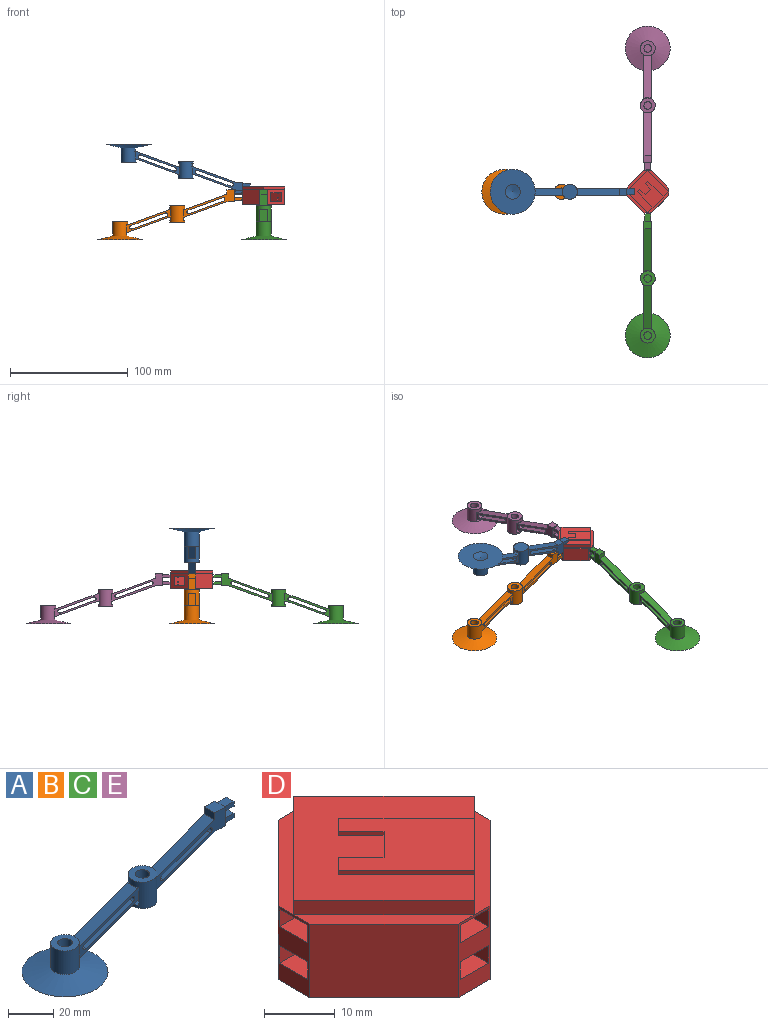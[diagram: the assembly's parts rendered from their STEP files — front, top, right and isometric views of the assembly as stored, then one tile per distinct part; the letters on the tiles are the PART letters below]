
ASSEMBLY  parts=5 mates=1
PART A: 57 faces, bbox 122.4x38.1x42.6 mm
  f0: cylinder r=6.35mm len=14.29mm, axis (0,0,-1), area 443.4mm2, adj f3,f4,f5,f18,f22,f24,f25,f28
  f1: cylinder r=6.35mm len=12.7mm, axis (0,0,-1), area 443.4mm2, adj f3,f4,f8,f9,f11,f12,f26,f27
  f2: cylinder r=3.23mm len=12.7mm, axis (0,0,-1), area 228.9mm2, adj f9,f10,f13,f26,f27
  f3: plane 37.5x19.38mm, normal (0,-1,0), area 137.5mm2, adj f0,f1,f5,f12,f13,f14,f15,f16
  f4: plane 37.5x19.38mm, normal (0,1,0), area 137.5mm2, adj f0,f1,f11,f13,f14,f15,f16,f17
  f5: plane 3.18x0.85mm, normal (0,0,1), area 0.9mm2, adj f0,f3,f19
  f6: cone r=0mm half-angle=76deg, axis (0,0,-1), area 130.6mm2, adj f7
  f7: plane 38.1x38.1mm, normal (0,0,-1), area 1013.4mm2, adj f6,f8
  f8: cone r=19.05mm half-angle=76deg, axis (0,0,-1), area 1044.6mm2, adj f1,f7,f10
  f9: plane 12.7x12.7mm, normal (0,0,1), area 94mm2, adj f1,f2
  f10: plane 9.58x6.45mm, normal (0,0,1), area 55mm2, adj f2,f8,f26,f27
  f11: plane 3.18x0.85mm, normal (0,0,1), area 0.9mm2, adj f1,f4,f19
  f12: plane 3.18x0.85mm, normal (0,0,1), area 0.9mm2, adj f1,f3,f19
  f13: plane 6.35x5.78mm, normal (0,0,-1), area 24mm2, adj f2,f3,f4,f20,f26,f27
  f14: cylinder r=1.49mm len=6.35mm, axis (0,1,0), area 29.8mm2, adj f3,f4,f15,f21
  f15: plane 29.5x10.74mm, normal (-0.34,0,0.94), area 199.3mm2, adj f3,f4,f14,f16
  f16: cylinder r=1.49mm len=6.35mm, axis (0,1,0), area 29.8mm2, adj f3,f4,f15,f21
  f17: plane 6.35x5.78mm, normal (0,0,-1), area 24mm2, adj f3,f4,f20,f23,f28,f29
  f18: plane 3.18x0.85mm, normal (0,0,1), area 0.9mm2, adj f0,f4,f19
  f19: plane 35.8x13.03mm, normal (-0.34,0,0.94), area 241.9mm2, adj f3,f4,f5,f11,f12,f18
  f20: plane 35.8x13.03mm, normal (0.34,0,-0.94), area 241.9mm2, adj f3,f4,f13,f17
  f21: plane 29.5x10.74mm, normal (0.34,0,-0.94), area 199.3mm2, adj f3,f4,f14,f16
  f22: plane 12.7x6.45mm, normal (0,0,1), area 77.2mm2, adj f0,f23,f28,f29,f30,f32
  f23: cylinder r=3.23mm len=12.7mm, axis (0,0,-1), area 200.3mm2, adj f17,f22,f24,f28,f29,f30,f31,f32
  f24: plane 12.7x12.7mm, normal (0,0,1), area 94mm2, adj f0,f23
  f25: plane 12.7x12.7mm, normal (0,0,-1), area 126.7mm2, adj f0
  f26: plane 4.93x3.18mm, normal (0,-1,0), area 15.6mm2, adj f1,f2,f10,f13
  f27: plane 4.93x3.18mm, normal (0,1,0), area 15.6mm2, adj f1,f2,f10,f13
  f28: plane 4.93x3.18mm, normal (0,1,0), area 15.6mm2, adj f0,f17,f22,f23
  f29: plane 4.93x3.18mm, normal (0,-1,0), area 15.6mm2, adj f0,f17,f22,f23
  f30: plane 4.93x3.18mm, normal (0,-1,0), area 15.6mm2, adj f0,f22,f23,f31
  f31: plane 6.35x5.78mm, normal (0,0,-1), area 24mm2, adj f23,f30,f32,f35,f36,f41
  f32: plane 4.93x3.18mm, normal (0,1,0), area 15.6mm2, adj f0,f22,f23,f31
  f33: plane 3.18x0.85mm, normal (0,0,1), area 0.9mm2, adj f0,f36,f45
  f34: plane 3.18x0.85mm, normal (0,0,1), area 0.9mm2, adj f0,f35,f45
  f35: plane 43x23.19mm, normal (0,-1,0), area 196.8mm2, adj f0,f31,f34,f37,f38,f39,f40,f41
  f36: plane 43x23.19mm, normal (0,1,0), area 196.8mm2, adj f0,f31,f33,f37,f38,f39,f40,f41
  f37: plane 10.16x6.35mm, normal (1,0,0), area 40.1mm2, adj f35,f36,f42,f43,f47,f48,f49,f50
  f38: cylinder r=1.49mm len=6.35mm, axis (0,1,0), area 29.8mm2, adj f35,f36,f39,f46
  f39: plane 29.45x10.72mm, normal (0.34,0,-0.94), area 199mm2, adj f35,f36,f38,f40
  f40: cylinder r=1.49mm len=6.35mm, axis (0,1,0), area 29.8mm2, adj f35,f36,f39,f46
  f41: plane 35.8x13.03mm, normal (0.34,0,-0.94), area 241.9mm2, adj f31,f35,f36,f42
  f42: plane 6.35x6.35mm, normal (0,0,-1), area 40.3mm2, adj f35,f36,f37,f41
  f43: plane 6.35x6.35mm, normal (0,0,1), area 40.3mm2, adj f35,f36,f37,f44
  f44: plane 6.35x3.81mm, normal (-1,0,0), area 24.2mm2, adj f35,f36,f43,f45
  f45: plane 35.8x13.03mm, normal (-0.34,0,0.94), area 241.9mm2, adj f33,f34,f35,f36,f44
  f46: plane 29.45x10.72mm, normal (-0.34,0,0.94), area 199mm2, adj f35,f36,f38,f40
  f47: plane 6.35x2.54mm, normal (0,1,0), area 16.1mm2, adj f37,f48,f50,f51
  f48: plane 6.35x4.82mm, normal (0,0,1), area 30.6mm2, adj f37,f47,f49,f51
  f49: plane 6.35x2.54mm, normal (0,-1,0), area 16.1mm2, adj f37,f48,f50,f51
  f50: plane 6.35x4.82mm, normal (0,0,-1), area 30.6mm2, adj f37,f47,f49,f51
  f51: plane 4.82x2.54mm, normal (1,0,0), area 12.2mm2, adj f47,f48,f49,f50
  f52: plane 6.35x2.54mm, normal (0,-1,0), area 16.1mm2, adj f37,f53,f55,f56
  f53: plane 6.35x4.82mm, normal (0,0,-1), area 30.6mm2, adj f37,f52,f54,f56
  f54: plane 6.35x2.54mm, normal (0,1,0), area 16.1mm2, adj f37,f53,f55,f56
  f55: plane 6.35x4.82mm, normal (0,0,1), area 30.6mm2, adj f37,f52,f54,f56
  f56: plane 4.82x2.54mm, normal (1,0,0), area 12.2mm2, adj f52,f53,f54,f55
PART B: same geometry as A
PART C: same geometry as A
PART D: 70 faces, bbox 35.9x35.9x15.9 mm
  f0: plane 6.6x5.59mm, normal (0,0,-1), area 36.8mm2, adj f1,f3,f15,f32,f66
  f1: plane 6.19x3.05mm, normal (0,-1,0), area 18.9mm2, adj f0,f2,f15,f66
  f2: plane 6.6x5.59mm, normal (0,0,1), area 36.8mm2, adj f1,f3,f15,f32,f66
  f3: plane 5.17x3.05mm, normal (-1,0,0), area 15.8mm2, adj f0,f2,f32,f66
  f4: plane 6.6x3.05mm, normal (0,-1,0), area 19.7mm2, adj f5,f6,f15,f34,f66,f68
  f5: plane 6.6x5.59mm, normal (0,0,1), area 36.8mm2, adj f4,f6,f15,f33,f66
  f6: plane 5.59x3.05mm, normal (-1,0,0), area 16.6mm2, adj f4,f5,f33,f34,f66,f68
  f7: plane 6.6x5.59mm, normal (0,0,-1), area 36.8mm2, adj f9,f10,f14,f45,f66
  f8: plane 6.6x5.59mm, normal (0,0,1), area 36.8mm2, adj f9,f10,f14,f45,f66
  f9: plane 6.19x3.05mm, normal (-1,0,0), area 18.9mm2, adj f7,f8,f14,f66
  f10: plane 5.17x3.05mm, normal (0,-1,0), area 15.8mm2, adj f7,f8,f45,f66
  f11: plane 6.6x5.59mm, normal (0,0,1), area 36.8mm2, adj f12,f13,f14,f46,f66
  f12: plane 6.6x3.05mm, normal (-1,0,0), area 19.7mm2, adj f11,f13,f14,f47,f66,f68
  f13: plane 5.59x3.05mm, normal (0,-1,0), area 16.6mm2, adj f11,f12,f46,f47,f66,f68
  f14: plane 12.7x6.35mm, normal (0,-1,0), area 46.6mm2, adj f7,f8,f9,f11,f12,f21,f26,f27
  f15: plane 12.7x6.35mm, normal (-1,0,0), area 46.6mm2, adj f0,f1,f2,f4,f5,f21,f26,f27
  f16: plane 17.96x17.96mm, normal (-0.71,0.71,0), area 64.5mm2, adj f17,f19,f20,f29
  f17: plane 17.96x17.96mm, normal (-0.71,-0.71,0), area 64.5mm2, adj f16,f18,f20,f27
  f18: plane 17.96x17.96mm, normal (0.71,-0.71,0), area 72.6mm2, adj f17,f19,f20,f31,f51,f52,f55
  f19: plane 17.96x17.96mm, normal (0.71,0.71,0), area 64.5mm2, adj f16,f18,f20,f25
  f20: plane 35.92x35.92mm, normal (0,0,1), area 443.5mm2, adj f16,f17,f18,f19,f48,f49,f50,f51
  f21: plane 35.92x35.92mm, normal (0,0,-1), area 853.1mm2, adj f14,f15,f22,f23,f24,f26,f28,f30
  f22: plane 12.7x6.35mm, normal (1,0,0), area 46.6mm2, adj f21,f23,f25,f30,f31,f35,f36,f37
  f23: plane 14.79x14.79mm, normal (0.71,0.71,0), area 265.6mm2, adj f21,f22,f24,f25
  f24: plane 12.7x6.35mm, normal (0,1,0), area 46.6mm2, adj f21,f23,f25,f28,f29,f56,f57,f58
  f25: plane 17.96x17.96mm, normal (0,0,1), area 52mm2, adj f19,f22,f23,f24
  f26: plane 14.79x14.79mm, normal (-0.71,-0.71,0), area 265.6mm2, adj f14,f15,f21,f27
  f27: plane 17.96x17.96mm, normal (0,0,1), area 52mm2, adj f14,f15,f17,f26
  f28: plane 14.79x14.79mm, normal (-0.71,0.71,0), area 164.7mm2, adj f15,f21,f24,f29,f66,f67,f68,f69
  f29: plane 17.96x17.96mm, normal (0,0,1), area 52mm2, adj f15,f16,f24,f28
  f30: plane 14.79x14.79mm, normal (0.71,-0.71,0), area 164.7mm2, adj f14,f21,f22,f31,f66,f67,f68,f69
  f31: plane 17.96x17.96mm, normal (0,0,1), area 52mm2, adj f14,f18,f22,f30
  f32: plane 6.6x3.05mm, normal (0,1,0), area 20.1mm2, adj f0,f2,f3,f15
  f33: plane 6.6x3.05mm, normal (0,1,0), area 20.1mm2, adj f5,f6,f15,f34
  f34: plane 6.6x5.59mm, normal (0,0,-1), area 36.9mm2, adj f4,f6,f15,f33
  f35: plane 6.6x5.59mm, normal (0,0,1), area 36.8mm2, adj f22,f36,f38,f39,f67
  f36: plane 6.6x3.05mm, normal (0,-1,0), area 20.1mm2, adj f22,f35,f37,f39
  f37: plane 6.6x5.59mm, normal (0,0,-1), area 36.8mm2, adj f22,f36,f38,f39,f67
  f38: plane 6.19x3.05mm, normal (0,1,0), area 18.9mm2, adj f22,f35,f37,f67
  f39: plane 5.17x3.05mm, normal (1,0,0), area 15.8mm2, adj f35,f36,f37,f67
  f40: plane 6.6x3.05mm, normal (0,1,0), area 19.7mm2, adj f22,f41,f43,f44,f67,f68
  f41: plane 6.6x5.59mm, normal (0,0,1), area 36.8mm2, adj f22,f40,f42,f44,f67
  f42: plane 6.6x3.05mm, normal (0,-1,0), area 20.1mm2, adj f22,f41,f43,f44
  f43: plane 6.6x5.59mm, normal (0,0,-1), area 36.9mm2, adj f22,f40,f42,f44
  f44: plane 5.59x3.05mm, normal (1,0,0), area 16.6mm2, adj f40,f41,f42,f43,f67,f68
  f45: plane 6.6x3.05mm, normal (1,0,0), area 20.1mm2, adj f7,f8,f10,f14
  f46: plane 6.6x3.05mm, normal (1,0,0), area 20.1mm2, adj f11,f13,f14,f47
  f47: plane 6.6x5.59mm, normal (0,0,-1), area 36.9mm2, adj f12,f13,f14,f46
  f48: plane 4.49x4.49mm, normal (-0.71,0.71,0), area 4mm2, adj f20,f49,f54,f55
  f49: plane 4.49x4.49mm, normal (0.71,0.71,0), area 4mm2, adj f20,f48,f50,f55
  f50: plane 2.25x2.25mm, normal (-0.71,0.71,0), area 2mm2, adj f20,f49,f51,f55
  f51: plane 13.47x13.47mm, normal (-0.71,-0.71,0), area 12.1mm2, adj f18,f20,f50,f55
  f52: plane 13.47x13.47mm, normal (0.71,0.71,0), area 12.1mm2, adj f18,f20,f53,f55
  f53: plane 2.25x2.25mm, normal (-0.71,0.71,0), area 2mm2, adj f20,f52,f54,f55
  f54: plane 4.49x4.49mm, normal (-0.71,-0.71,0), area 4mm2, adj f20,f48,f53,f55
  f55: plane 22.45x22.45mm, normal (0,0,1), area 201.6mm2, adj f18,f48,f49,f50,f51,f52,f53,f54
  f56: plane 6.6x5.59mm, normal (0,0,1), area 36.8mm2, adj f24,f57,f59,f60,f67
  f57: plane 6.19x3.05mm, normal (1,0,0), area 18.9mm2, adj f24,f56,f58,f67
  f58: plane 6.6x5.59mm, normal (0,0,-1), area 36.8mm2, adj f24,f57,f59,f60,f67
  f59: plane 6.6x3.05mm, normal (-1,0,0), area 20.1mm2, adj f24,f56,f58,f60
  f60: plane 5.17x3.05mm, normal (0,1,0), area 15.8mm2, adj f56,f58,f59,f67
  f61: plane 6.6x3.05mm, normal (-1,0,0), area 20.1mm2, adj f24,f62,f64,f65
  f62: plane 6.6x5.59mm, normal (0,0,1), area 36.8mm2, adj f24,f61,f63,f65,f67
  f63: plane 6.6x3.05mm, normal (1,0,0), area 19.7mm2, adj f24,f62,f64,f65,f67,f68
  f64: plane 6.6x5.59mm, normal (0,0,-1), area 36.9mm2, adj f24,f61,f63,f65
  f65: plane 5.59x3.05mm, normal (0,1,0), area 16.6mm2, adj f61,f62,f63,f64,f67,f68
  f66: plane 21.14x21.14mm, normal (0.71,0.71,0), area 232.4mm2, adj f0,f1,f2,f3,f4,f5,f6,f7
  f67: plane 21.14x21.14mm, normal (-0.71,-0.71,0), area 232.4mm2, adj f28,f30,f35,f37,f38,f39,f40,f41
  f68: plane 30.12x30.12mm, normal (0,0,-1), area 379.3mm2, adj f4,f6,f12,f13,f28,f30,f40,f44
  f69: plane 30.12x30.12mm, normal (0,0,1), area 379.6mm2, adj f28,f30,f66,f67
PART E: same geometry as A
PLACE A rot(axis=(-1,0,0),180deg) t=(-114.71,-0.07,51.52)mm
PLACE B t=(-121.9,0,-29.84)mm
PLACE C rot(axis=(0,0,1),90deg) t=(0,-122.15,-29.84)mm
PLACE D at identity fixed
PLACE E rot(axis=(0,0,-1),90deg) t=(0,121.9,-29.84)mm
MATE fastened A.f51 <-> D.f6  axis (1,0,0) through (-11.36,-0.07,10.85)mm
